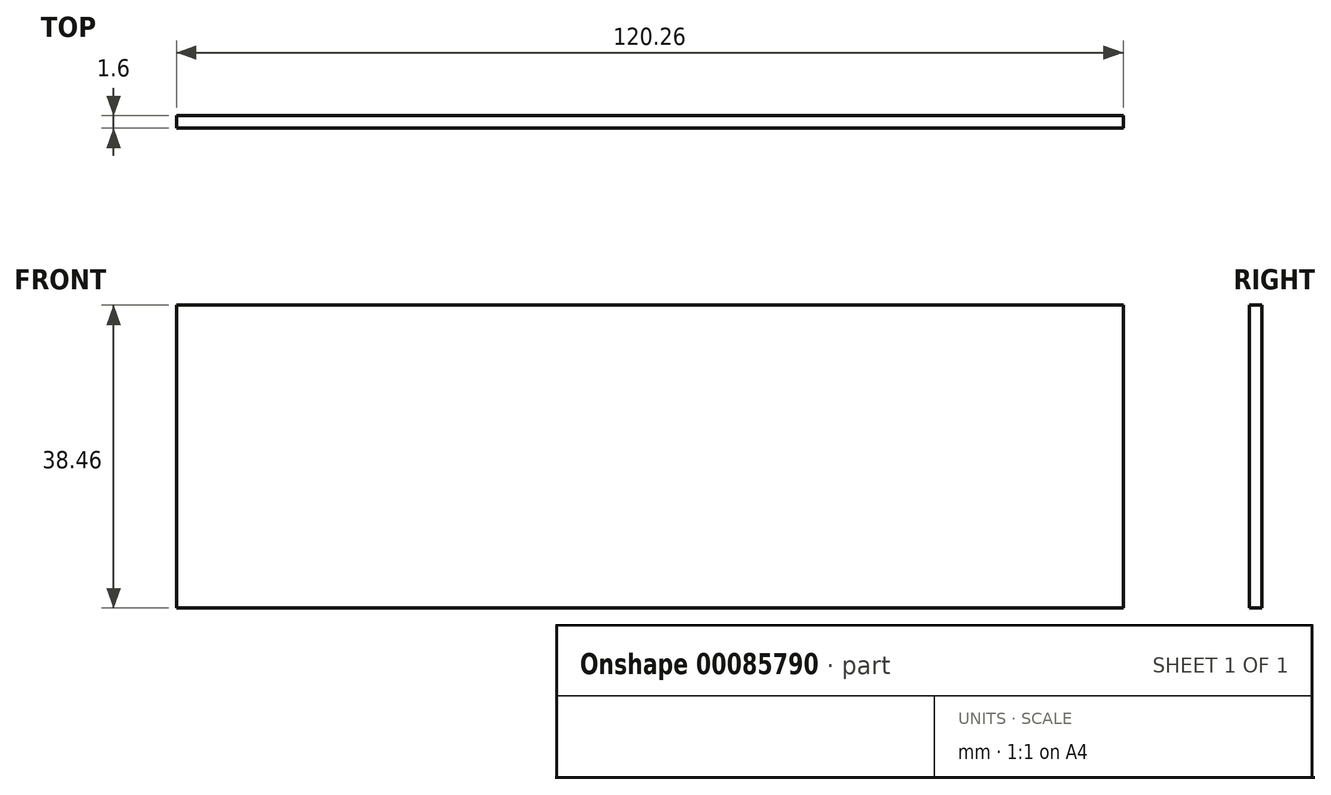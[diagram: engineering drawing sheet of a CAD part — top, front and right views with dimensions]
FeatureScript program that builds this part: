
annotation { "Feature Type Name" : "Feature", "Feature Type Description" : "" }
export const myFeature = defineFeature(function(context is Context, id is Id, definition is map)
    precondition{}
    {
        {
            var Q0;
            Q0=qCreatedBy(makeId("Front.planeOp"),FACE);
            var sketch = newSketch(context, id + "F0", { "sketchPlane" : qUnion([Q0])});
            skLineSegment(sketch, "E0.bottom", {"start": v(60.13, -19.23) * mm, "end": v(-60.13, -19.23) * mm});
            skLineSegment(sketch, "E0.top", {"start": v(60.13, 19.23) * mm, "end": v(-60.13, 19.23) * mm});
            skLineSegment(sketch, "E0.left", {"start": v(60.13, -19.23) * mm, "end": v(60.13, 19.23) * mm});
            skLineSegment(sketch, "E0.right", {"start": v(-60.13, -19.23) * mm, "end": v(-60.13, 19.23) * mm});
            skPoint(sketch, "E0.middle", {"position": v(0, 0) * mm});
            skSolve(sketch);
        }
        {
            var Q0;
            Q0=makeQuery(id+"F0.imprint","IMPRINT",FACE,{"disambiguationData":[TD([[makeQuery(id+"F0.imprint","IMPRINT",EDGE,{"derivedFrom":sQuery(id+"F0.wireOp",EDGE,"E0.bottom")}),-1.0]])]});
            extrude(context, id + "F1", {"entities" : qUnion([Q0]), "depth" : 1.6 * mm});
        }
    });
